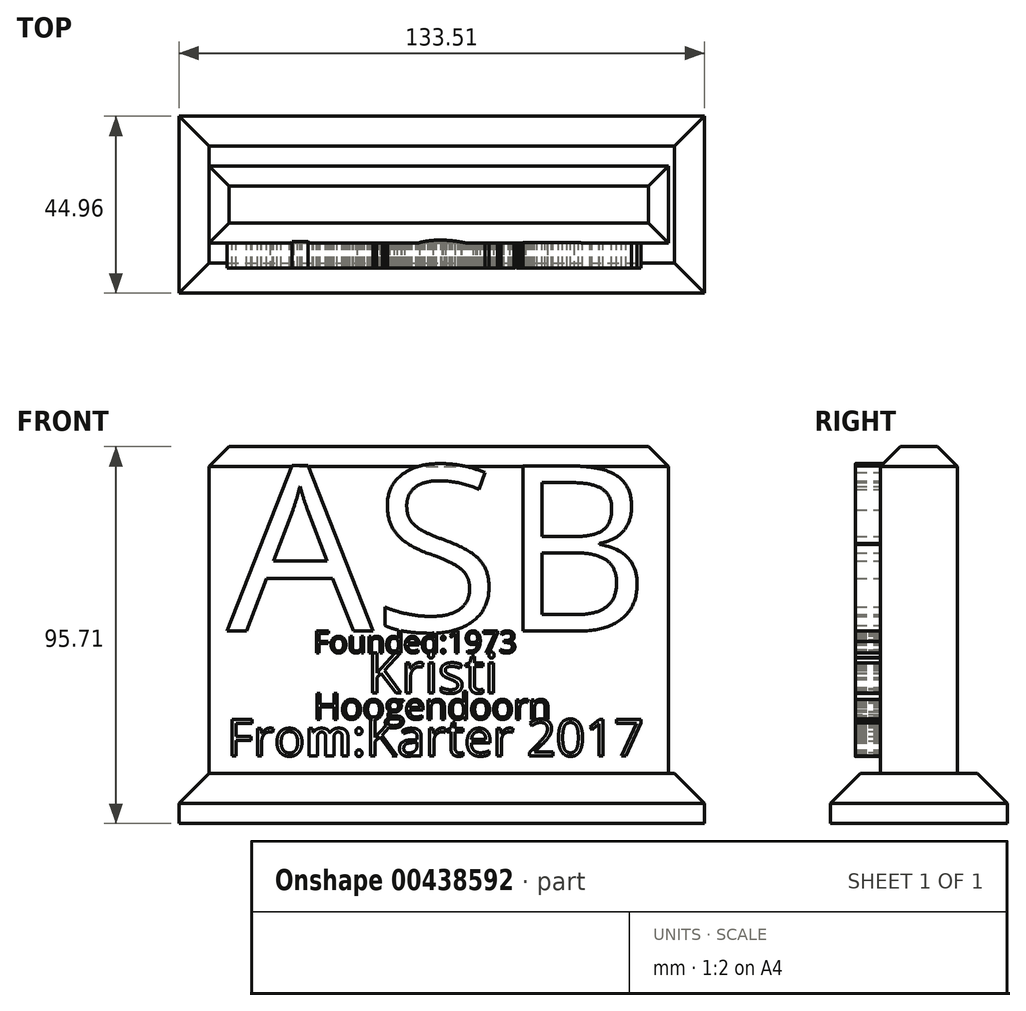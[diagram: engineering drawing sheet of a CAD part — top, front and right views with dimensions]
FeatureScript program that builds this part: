
annotation { "Feature Type Name" : "Feature", "Feature Type Description" : "" }
export const myFeature = defineFeature(function(context is Context, id is Id, definition is map)
    precondition{}
    {
        {
            var Q0;
            Q0=qCreatedBy(makeId("Front.planeOp"),FACE);
            var sketch = newSketch(context, id + "F0", { "sketchPlane" : qUnion([Q0])});
            skLineSegment(sketch, "E0.bottom", {"start": v(-54, 0) * mm, "end": v(54, 0) * mm});
            skLineSegment(sketch, "E0.top", {"start": v(-54, -74.02) * mm, "end": v(54, -74.02) * mm});
            skText(sketch, "E1", { "text": "ASB", "fontName": "OpenSans-Regular.ttf"});
            skText(sketch, "E2", { "text": "Founded:1973", "fontName": "OpenSans-Regular.ttf"});
            skText(sketch, "E3", { "text": "Kristi", "fontName": "OpenSans-Regular.ttf"});
            skText(sketch, "E4", { "text": "Hoogendoorn", "fontName": "OpenSans-Regular.ttf"});
            skText(sketch, "E5", { "text": "From:Karter 2017", "fontName": "OpenSans-Regular.ttf"});
            const initialGuessF0  = {"E1": [-0.054, -0.04228, 1, 0, 0.04228], "E2": [-0.03196, -0.04783, 1, 0, 0.00555], "E3": [-0.01842, -0.05804, 1, 0, 0.0102], "E4": [-0.03196, -0.0647, 1, 0, 0.00666], "E5": [-0.054, -0.07402, 1, 0, 0.00932]};
            skSetInitialGuess(sketch, initialGuessF0);
            skSolve(sketch);
        }
        {
            var Q0;
            Q0=qCreatedBy(makeId("Front.planeOp"),FACE);
            var sketch = newSketch(context, id + "F1", { "sketchPlane" : qUnion([Q0])});
            skLineSegment(sketch, "E6.bottom", {"start": v(-58.6, 4.55) * mm, "end": v(58.15, 4.55) * mm});
            skLineSegment(sketch, "E6.top", {"start": v(-58.6, -78.46) * mm, "end": v(58.15, -78.46) * mm});
            skLineSegment(sketch, "E6.left", {"start": v(-58.6, 4.55) * mm, "end": v(-58.6, -78.46) * mm});
            skLineSegment(sketch, "E6.right", {"start": v(58.15, 4.55) * mm, "end": v(58.15, -78.46) * mm});
            skSolve(sketch);
        }
        {
            var Q0;
            Q0 = qSketchRegion(id + "F1", true);
            extrude(context, id + "F2", {"entities" : qUnion([Q0]), "depth" : 12.7 * mm, "hasSecondDirection" : true, "secondDirectionOppositeDirection" : true, "secondDirectionDepth" : 6.86 * mm, "offsetDistance" : 25.4 * mm});
        }
        {
            var Q0;
            Q0 = qSketchRegion(id + "F0", true);
            extrude(context, id + "F3", {"entities" : qUnion([Q0]), "operationType" : NewBodyOperationType.ADD, "depth" : 19.05 * mm});
        }
        {
            var Q0;
            Q0=makeQuery(id+"F3.opExtrude","CAP_FACE",FACE,{"disambiguationData":[OSD([sQuery(id+"F0.wireOp",EDGE,"E1.sketch_text.stroke-0"),sQuery(id+"F0.wireOp",EDGE,"E1.sketch_text.stroke-1"),sQuery(id+"F0.wireOp",EDGE,"E1.sketch_text.stroke-2"),sQuery(id+"F0.wireOp",EDGE,"E1.sketch_text.stroke-3"),sQuery(id+"F0.wireOp",EDGE,"E1.sketch_text.stroke-4"),sQuery(id+"F0.wireOp",EDGE,"E1.sketch_text.stroke-5"),sQuery(id+"F0.wireOp",EDGE,"E1.sketch_text.stroke-6"),sQuery(id+"F0.wireOp",EDGE,"E1.sketch_text.stroke-7"),sQuery(id+"F0.wireOp",EDGE,"E1.sketch_text.stroke-8"),sQuery(id+"F0.wireOp",EDGE,"E1.sketch_text.stroke-9"),sQuery(id+"F0.wireOp",EDGE,"E1.sketch_text.stroke-10"),sQuery(id+"F0.wireOp",EDGE,"E1.sketch_text.stroke-11"),sQuery(id+"F0.wireOp",EDGE,"E1.sketch_text.stroke-12")])],"isStart":false});
            var sketch = newSketch(context, id + "F4", { "sketchPlane" : qUnion([Q0])});
            skLineSegment(sketch, "E7", {"start": v(-27.84, -68.14) * mm, "end": v(-27.84, -74.04) * mm});
            skLineSegment(sketch, "E8", {"start": v(-30.96, -74.07) * mm, "end": v(-30.96, -69) * mm});
            skLineSegment(sketch, "E9", {"start": v(-30.96, -74.07) * mm, "end": v(-28.92, -74.07) * mm});
            skLineSegment(sketch, "E10", {"start": v(-28.92, -74.07) * mm, "end": v(-28.92, -69) * mm});
            skArc(sketch, "E11", {"start": v(-28.92, -69) * mm, "mid": v(-29.94, -67.97) * mm, "end": v(-30.96, -69) * mm});
            skLineSegment(sketch, "E12.MirrorCS", {"start": v(-26.75, -74.07) * mm, "end": v(-26.75, -69) * mm});
            skLineSegment(sketch, "E13.MirrorCS", {"start": v(-24.71, -74.07) * mm, "end": v(-24.71, -69) * mm});
            skLineSegment(sketch, "E14.MirrorCS", {"start": v(-24.71, -74.07) * mm, "end": v(-26.75, -74.07) * mm});
            skArc(sketch, "E15.MirrorCS", {"start": v(-26.75, -69) * mm, "mid": v(-25.73, -67.97) * mm, "end": v(-24.71, -69) * mm});
            skSolve(sketch);
        }
        {
            var Q0;
            Q0=makeQuery(id+"F4.imprint","IMPRINT",FACE,{"disambiguationData":[TD([[makeQuery(id+"F4.imprint","IMPRINT",EDGE,{"derivedFrom":sQuery(id+"F4.wireOp",EDGE,"E8")}),-1.0]])]});
            var Q1;
            Q1=makeQuery(id+"F4.imprint","IMPRINT",FACE,{"disambiguationData":[TD([[makeQuery(id+"F4.imprint","IMPRINT",EDGE,{"derivedFrom":sQuery(id+"F4.wireOp",EDGE,"E12.MirrorCS")}),-1.0]])]});
            extrude(context, id + "F5", {"entities" : qUnion([Q0, Q1]), "operationType" : NewBodyOperationType.REMOVE, "oppositeDirection" : true, "depth" : 6.35 * mm});
        }
        {
            var Q0;
            Q0=makeQuery(id+"F3.opExtrude","CAP_FACE",FACE,{"disambiguationData":[OSD([sQuery(id+"F0.wireOp",EDGE,"E0.top"),sQuery(id+"F0.wireOp",EDGE,"E4.sketch_text.stroke-29"),sQuery(id+"F0.wireOp",EDGE,"E4.sketch_text.stroke-30"),sQuery(id+"F0.wireOp",EDGE,"E4.sketch_text.stroke-31"),sQuery(id+"F0.wireOp",EDGE,"E4.sketch_text.stroke-32"),sQuery(id+"F0.wireOp",EDGE,"E4.sketch_text.stroke-33"),sQuery(id+"F0.wireOp",EDGE,"E4.sketch_text.stroke-34"),sQuery(id+"F0.wireOp",EDGE,"E4.sketch_text.stroke-35"),sQuery(id+"F0.wireOp",EDGE,"E4.sketch_text.stroke-36"),sQuery(id+"F0.wireOp",EDGE,"E4.sketch_text.stroke-37"),sQuery(id+"F0.wireOp",EDGE,"E4.sketch_text.stroke-38"),sQuery(id+"F0.wireOp",EDGE,"E4.sketch_text.stroke-39"),sQuery(id+"F0.wireOp",EDGE,"E4.sketch_text.stroke-40"),sQuery(id+"F0.wireOp",EDGE,"E4.sketch_text.stroke-41"),sQuery(id+"F0.wireOp",EDGE,"E4.sketch_text.stroke-42"),sQuery(id+"F0.wireOp",EDGE,"E4.sketch_text.stroke-43"),sQuery(id+"F0.wireOp",EDGE,"E4.sketch_text.stroke-44"),sQuery(id+"F0.wireOp",EDGE,"E4.sketch_text.stroke-45"),sQuery(id+"F0.wireOp",EDGE,"E4.sketch_text.stroke-46"),sQuery(id+"F0.wireOp",EDGE,"E4.sketch_text.stroke-47"),sQuery(id+"F0.wireOp",EDGE,"E4.sketch_text.stroke-48"),sQuery(id+"F0.wireOp",EDGE,"E4.sketch_text.stroke-49"),sQuery(id+"F0.wireOp",EDGE,"E4.sketch_text.stroke-50"),sQuery(id+"F0.wireOp",EDGE,"E4.sketch_text.stroke-51"),sQuery(id+"F0.wireOp",EDGE,"E4.sketch_text.stroke-52"),sQuery(id+"F0.wireOp",EDGE,"E4.sketch_text.stroke-53"),sQuery(id+"F0.wireOp",EDGE,"E4.sketch_text.stroke-54"),sQuery(id+"F0.wireOp",EDGE,"E4.sketch_text.stroke-55"),sQuery(id+"F0.wireOp",EDGE,"E4.sketch_text.stroke-56"),sQuery(id+"F0.wireOp",EDGE,"E4.sketch_text.stroke-57"),sQuery(id+"F0.wireOp",EDGE,"E4.sketch_text.stroke-58"),sQuery(id+"F0.wireOp",EDGE,"E4.sketch_text.stroke-59"),sQuery(id+"F0.wireOp",EDGE,"E4.sketch_text.stroke-60"),sQuery(id+"F0.wireOp",EDGE,"E4.sketch_text.stroke-61"),sQuery(id+"F0.wireOp",EDGE,"E4.sketch_text.stroke-62"),sQuery(id+"F0.wireOp",EDGE,"E4.sketch_text.stroke-63"),sQuery(id+"F0.wireOp",EDGE,"E4.sketch_text.stroke-64"),sQuery(id+"F0.wireOp",EDGE,"E4.sketch_text.stroke-65"),sQuery(id+"F0.wireOp",EDGE,"E4.sketch_text.stroke-66"),sQuery(id+"F0.wireOp",EDGE,"E4.sketch_text.stroke-67"),sQuery(id+"F0.wireOp",EDGE,"E4.sketch_text.stroke-68"),sQuery(id+"F0.wireOp",EDGE,"E4.sketch_text.stroke-69"),sQuery(id+"F0.wireOp",EDGE,"E4.sketch_text.stroke-70"),sQuery(id+"F0.wireOp",EDGE,"E4.sketch_text.stroke-71"),sQuery(id+"F0.wireOp",EDGE,"E4.sketch_text.stroke-72"),sQuery(id+"F0.wireOp",EDGE,"E4.sketch_text.stroke-73"),sQuery(id+"F0.wireOp",EDGE,"E4.sketch_text.stroke-74"),sQuery(id+"F0.wireOp",EDGE,"E4.sketch_text.stroke-75"),sQuery(id+"F0.wireOp",EDGE,"E4.sketch_text.stroke-76"),sQuery(id+"F0.wireOp",EDGE,"E4.sketch_text.stroke-77"),sQuery(id+"F0.wireOp",EDGE,"E4.sketch_text.stroke-78"),sQuery(id+"F0.wireOp",EDGE,"E4.sketch_text.stroke-79"),sQuery(id+"F0.wireOp",EDGE,"E4.sketch_text.stroke-80"),sQuery(id+"F0.wireOp",EDGE,"E4.sketch_text.stroke-81"),sQuery(id+"F0.wireOp",EDGE,"E4.sketch_text.stroke-82"),sQuery(id+"F0.wireOp",EDGE,"E4.sketch_text.stroke-83"),sQuery(id+"F0.wireOp",EDGE,"E4.sketch_text.stroke-84"),sQuery(id+"F0.wireOp",EDGE,"E4.sketch_text.stroke-85"),sQuery(id+"F0.wireOp",EDGE,"E4.sketch_text.stroke-86"),sQuery(id+"F0.wireOp",EDGE,"E4.sketch_text.stroke-87"),sQuery(id+"F0.wireOp",EDGE,"E4.sketch_text.stroke-88"),sQuery(id+"F0.wireOp",EDGE,"E4.sketch_text.stroke-89"),sQuery(id+"F0.wireOp",EDGE,"E5.sketch_text.stroke-82"),sQuery(id+"F0.wireOp",EDGE,"E5.sketch_text.stroke-86"),sQuery(id+"F0.wireOp",EDGE,"E5.sketch_text.stroke-87"),sQuery(id+"F0.wireOp",EDGE,"E5.sketch_text.stroke-88"),sQuery(id+"F0.wireOp",EDGE,"E5.sketch_text.stroke-89"),sQuery(id+"F0.wireOp",EDGE,"E5.sketch_text.stroke-90"),sQuery(id+"F0.wireOp",EDGE,"E5.sketch_text.stroke-92"),sQuery(id+"F0.wireOp",EDGE,"E5.sketch_text.stroke-93")])],"isStart":false});
            var sketch = newSketch(context, id + "F6", { "sketchPlane" : qUnion([Q0])});
            skText(sketch, "E16", { "text": "K", "fontName": "OpenSans-Regular.ttf"});
            skLineSegment(sketch, "E17", {"start": v(-17.46, -74.02) * mm, "end": v(-16.39, -74.02) * mm});
            skLineSegment(sketch, "E18", {"start": v(-16.39, -74.02) * mm, "end": v(-16.39, -70.29) * mm});
            skLineSegment(sketch, "E19", {"start": v(-16.39, -70.29) * mm, "end": v(-15.16, -69.21) * mm});
            skLineSegment(sketch, "E20", {"start": v(-15.16, -69.21) * mm, "end": v(-11.54, -74.02) * mm});
            skLineSegment(sketch, "E21", {"start": v(-11.54, -74.02) * mm, "end": v(-16.39, -74.02) * mm});
            const initialGuessF6  = {"E16": [-0.02052, -0.09139, 1, 0, 0.01007]};
            skSetInitialGuess(sketch, initialGuessF6);
            skSolve(sketch);
        }
        {
            var Q0;
            Q0 = qSketchRegion(id + "F6", true);
            extrude(context, id + "F7", {"entities" : qUnion([Q0]), "operationType" : NewBodyOperationType.REMOVE, "oppositeDirection" : true, "depth" : 6.35 * mm});
        }
        {
            var Q0;
            Q0=makeQuery(id+"F2.opExtrude","SWEPT_FACE",FACE,{"disambiguationData":[OSD([sQuery(id+"F1.wireOp",EDGE,"E6.top")])]});
            var sketch = newSketch(context, id + "F8", { "sketchPlane" : qUnion([Q0])});
            skLineSegment(sketch, "E22", {"start": v(-58.6, 25.4) * mm, "end": v(-66.21, 25.4) * mm});
            skLineSegment(sketch, "E23", {"start": v(58.15, 25.4) * mm, "end": v(67.3, 25.4) * mm});
            skLineSegment(sketch, "E24", {"start": v(-66.21, 25.4) * mm, "end": v(-66.21, -19.56) * mm});
            skLineSegment(sketch, "E25", {"start": v(-66.21, -19.56) * mm, "end": v(67.3, -19.56) * mm});
            skLineSegment(sketch, "E26", {"start": v(67.3, -19.56) * mm, "end": v(67.3, 25.4) * mm});
            skLineSegment(sketch, "E27", {"start": v(-58.6, 25.4) * mm, "end": v(58.15, 25.4) * mm});
            skSolve(sketch);
        }
        {
            var Q0;
            Q0 = qSketchRegion(id + "F8", true);
            extrude(context, id + "F9", {"entities" : qUnion([Q0]), "operationType" : NewBodyOperationType.ADD, "depth" : 12.7 * mm, "offsetDistance" : 25.4 * mm});
        }
        {
            var Q0;
            Q0=makeQuery(id+"F9.opExtrude","CAP_EDGE",EDGE,{"disambiguationData":[OSD([sQuery(id+"F8.wireOp",EDGE,"E22"),sQuery(id+"F8.wireOp",EDGE,"E23"),sQuery(id+"F8.wireOp",EDGE,"E27")])],"isStart":true});
            var Q1;
            Q1=makeQuery(id+"F9.opExtrude","CAP_EDGE",EDGE,{"disambiguationData":[OSD([sQuery(id+"F8.wireOp",EDGE,"E26")])],"isStart":true});
            var Q2;
            Q2=makeQuery(id+"F9.opExtrude","CAP_EDGE",EDGE,{"disambiguationData":[OSD([sQuery(id+"F8.wireOp",EDGE,"E25")])],"isStart":true});
            var Q3;
            Q3=makeQuery(id+"F9.opExtrude","CAP_EDGE",EDGE,{"disambiguationData":[OSD([sQuery(id+"F8.wireOp",EDGE,"E24")])],"isStart":true});
            chamfer(context, id + "F10", {"entities" : qUnion([Q0, Q1, Q2, Q3]), "width" : 7.62 * mm, "tangentPropagation" : true});
        }
        {
            var Q0;
            Q0=makeQuery(id+"F2.opExtrude","SWEPT_EDGE",EDGE,{"disambiguationData":[OSD([sQuery(id+"F1.wireOp",EDGE,"E6.bottom"),sQuery(id+"F1.wireOp",EDGE,"E6.right")])]});
            var Q1;
            Q1=makeQuery(id+"F2.opExtrude","CAP_EDGE",EDGE,{"disambiguationData":[OSD([sQuery(id+"F1.wireOp",EDGE,"E6.bottom")])],"isStart":false});
            var Q2;
            Q2=makeQuery(id+"F2.opExtrude","CAP_EDGE",EDGE,{"disambiguationData":[OSD([sQuery(id+"F1.wireOp",EDGE,"E6.bottom")])],"isStart":true});
            var Q3;
            Q3=makeQuery(id+"F2.opExtrude","SWEPT_EDGE",EDGE,{"disambiguationData":[OSD([sQuery(id+"F1.wireOp",EDGE,"E6.bottom"),sQuery(id+"F1.wireOp",EDGE,"E6.left")])]});
            chamfer(context, id + "F11", {"entities" : qUnion([Q0, Q1, Q2, Q3]), "width" : 5.08 * mm, "tangentPropagation" : true});
        }
    });
